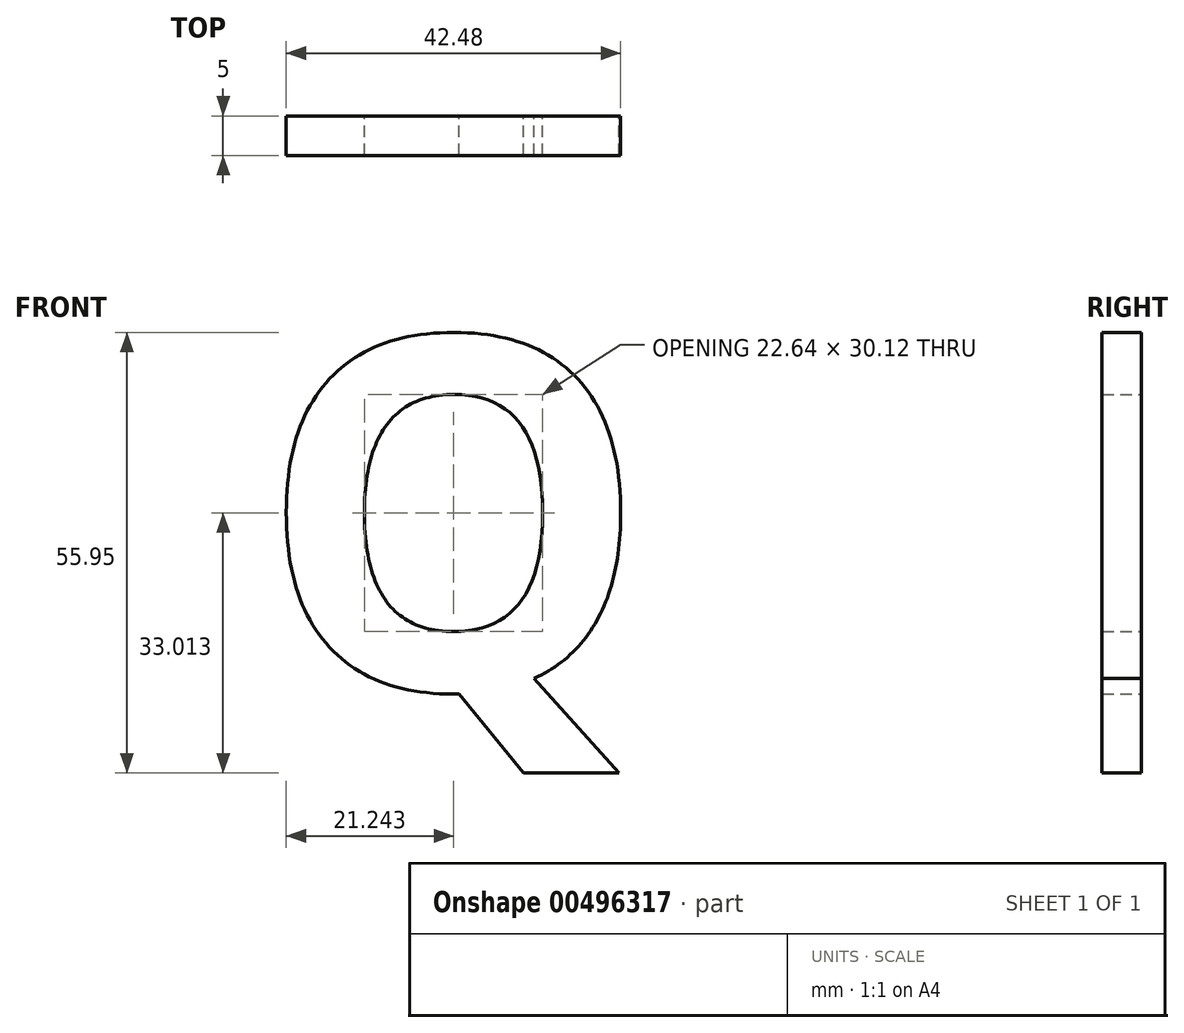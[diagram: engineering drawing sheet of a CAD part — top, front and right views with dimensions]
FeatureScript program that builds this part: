
annotation { "Feature Type Name" : "Feature", "Feature Type Description" : "" }
export const myFeature = defineFeature(function(context is Context, id is Id, definition is map)
    precondition{}
    {
        {
            var Q0;
            Q0=qCreatedBy(makeId("Front.planeOp"),FACE);
            var sketch = newSketch(context, id + "F0", { "sketchPlane" : qUnion([Q0])});
            skText(sketch, "E0", { "text": "Q", "fontName": "OpenSans-Bold.ttf"});
            const initialGuessF0  = {"E0": [-0.05581, 0.01417, 1, 0, 0.045]};
            skSetInitialGuess(sketch, initialGuessF0);
            skSolve(sketch);
        }
        {
            var Q0;
            Q0=makeQuery(id+"F0.imprint","IMPRINT",FACE,{"disambiguationData":[TD([[makeQuery(id+"F0.imprint","IMPRINT",EDGE,{"derivedFrom":sQuery(id+"F0.wireOp",EDGE,"E0.sketch_text.stroke-0")}),-1.0]])]});
            extrude(context, id + "F1", {"entities" : qUnion([Q0]), "depth" : 5 * mm});
        }
    });
